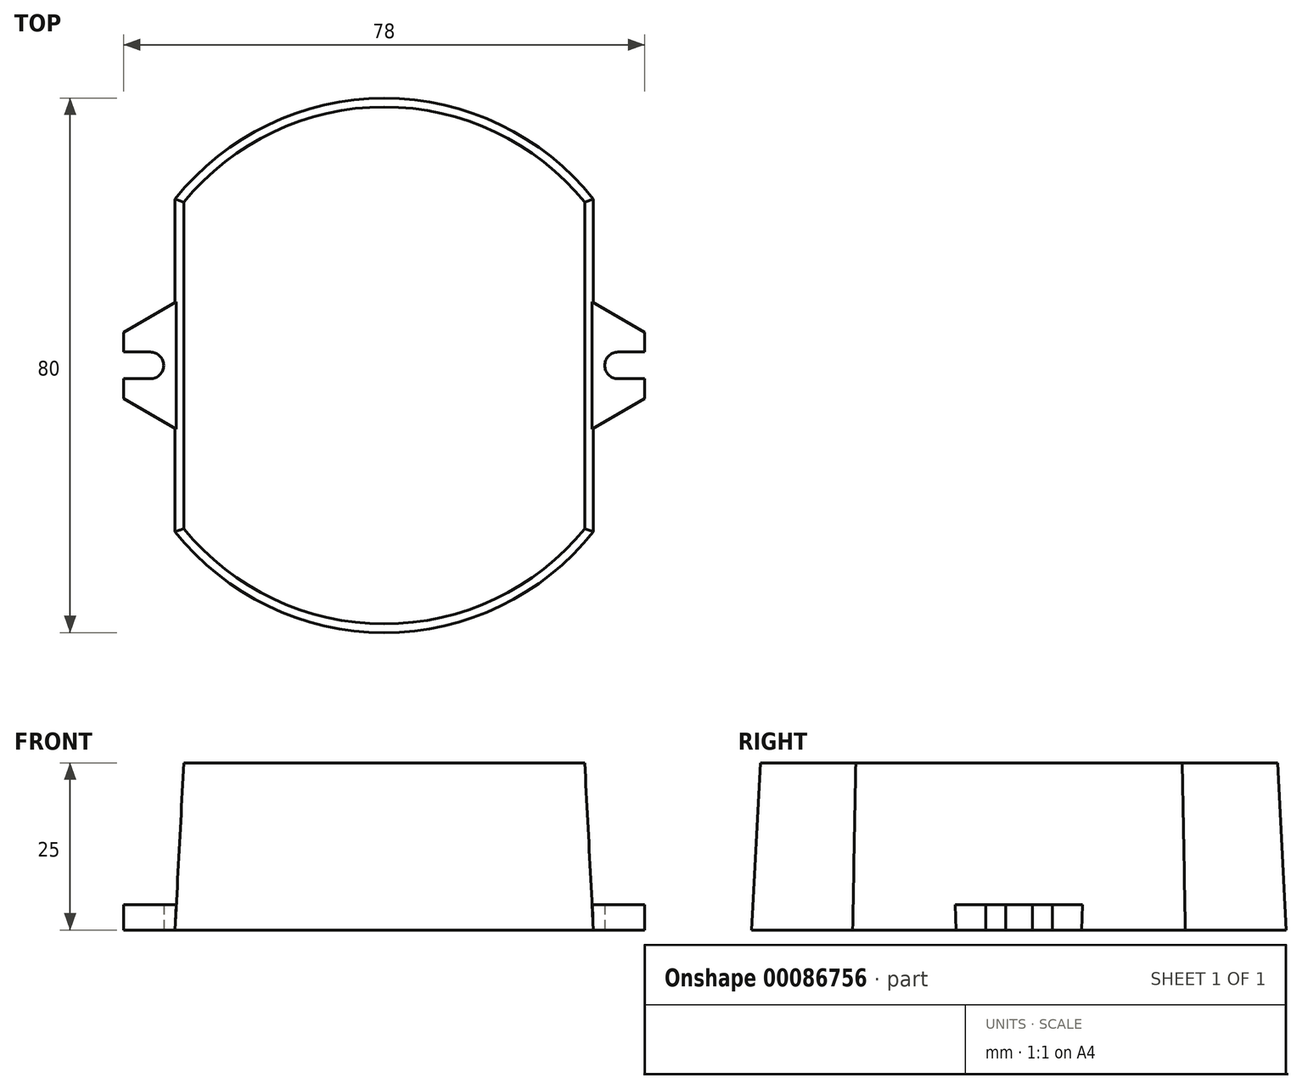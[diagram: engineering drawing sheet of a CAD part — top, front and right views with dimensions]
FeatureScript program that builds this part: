
annotation { "Feature Type Name" : "Feature", "Feature Type Description" : "" }
export const myFeature = defineFeature(function(context is Context, id is Id, definition is map)
    precondition{}
    {
        {
            var Q0;
            Q0=qCreatedBy(makeId("Top.planeOp"),FACE);
            var sketch = newSketch(context, id + "F0", { "sketchPlane" : qUnion([Q0])});
            skCircle(sketch, "E0", {"center": v(0, 0) * mm, "radius": 40 * mm});
            skSolve(sketch);
        }
        {
            var Q0;
            Q0 = qSketchRegion(id + "F0", true);
            extrude(context, id + "F1", {"entities" : qUnion([Q0]), "depth" : 25 * mm, "hasDraft" : true, "draftAngle" : 3 * degree, "draftPullDirection" : true});
        }
        {
            var Q0;
            Q0=makeQuery(id+"F1.opExtrude","CAP_FACE",FACE,{"disambiguationData":[OSD([sQuery(id+"F0.wireOp",EDGE,"E0")])],"isStart":false});
            var sketch = newSketch(context, id + "F2", { "sketchPlane" : qUnion([Q0])});
            skLineSegment(sketch, "E1.bottom", {"start": v(-30, 50.8) * mm, "end": v(-55.4, 50.8) * mm});
            skLineSegment(sketch, "E1.top", {"start": v(-30, -50.8) * mm, "end": v(-55.4, -50.8) * mm});
            skLineSegment(sketch, "E1.left", {"start": v(-30, 50.8) * mm, "end": v(-30, -50.8) * mm});
            skLineSegment(sketch, "E1.right", {"start": v(-55.4, 50.8) * mm, "end": v(-55.4, -50.8) * mm});
            skLineSegment(sketch, "E2", {"start": v(0, 0) * mm, "end": v(-67.46, 0) * mm, "construction": true});
            skLineSegment(sketch, "E3", {"start": v(0, 0) * mm, "end": v(0, 59.02) * mm, "construction": true});
            skLineSegment(sketch, "E4.MirrorCS", {"start": v(0, 0) * mm, "end": v(67.46, 0) * mm, "construction": true});
            skLineSegment(sketch, "E5.MirrorCS", {"start": v(55.4, 50.8) * mm, "end": v(55.4, -50.8) * mm});
            skLineSegment(sketch, "E6.MirrorCS", {"start": v(30, 50.8) * mm, "end": v(55.4, 50.8) * mm});
            skLineSegment(sketch, "E7.MirrorCS", {"start": v(30, 50.8) * mm, "end": v(30, -50.8) * mm});
            skLineSegment(sketch, "E8.MirrorCS", {"start": v(30, -50.8) * mm, "end": v(55.4, -50.8) * mm});
            skSolve(sketch);
        }
        {
            var Q0;
            Q0 = qSketchRegion(id + "F2", true);
            extrude(context, id + "F3", {"entities" : qUnion([Q0]), "operationType" : NewBodyOperationType.REMOVE, "endBound" : BoundingType.THROUGH_ALL, "oppositeDirection" : true, "depth" : 25.4 * mm, "hasDraft" : true, "draftAngle" : 3 * degree, "draftPullDirection" : true});
        }
        {
            var Q0;
            Q0=makeQuery(id+"F1.opExtrude","CAP_FACE",FACE,{"disambiguationData":[OSD([sQuery(id+"F0.wireOp",EDGE,"E0")])],"isStart":true});
            var sketch = newSketch(context, id + "F4", { "sketchPlane" : qUnion([Q0])});
            skLineSegment(sketch, "E9", {"start": v(0, 0) * mm, "end": v(0, -36.6) * mm, "construction": true});
            skArc(sketch, "E10", {"start": v(-33, 0) * mm, "mid": v(-33.59, 1.41) * mm, "end": v(-35, 2) * mm});
            skLineSegment(sketch, "E11", {"start": v(-35, 2) * mm, "end": v(-39, 2) * mm});
            skLineSegment(sketch, "E12", {"start": v(-39, 2) * mm, "end": v(-39, 4.96) * mm});
            skLineSegment(sketch, "E13", {"start": v(-39, 4.96) * mm, "end": v(-30, 10.16) * mm});
            skLineSegment(sketch, "E14", {"start": v(0, 0) * mm, "end": v(-53.11, 0) * mm, "construction": true});
            skArc(sketch, "E15.MirrorCS", {"start": v(-33, 0) * mm, "mid": v(-33.59, -1.41) * mm, "end": v(-35, -2) * mm});
            skLineSegment(sketch, "E16.MirrorCS", {"start": v(-39, -2) * mm, "end": v(-39, -4.96) * mm});
            skLineSegment(sketch, "E17.MirrorCS", {"start": v(-39, -4.96) * mm, "end": v(-30, -10.16) * mm});
            skLineSegment(sketch, "E18.MirrorCS", {"start": v(-35, -2) * mm, "end": v(-39, -2) * mm});
            skLineSegment(sketch, "E19", {"start": v(-30, -10.16) * mm, "end": v(-30, 10.16) * mm});
            skLineSegment(sketch, "E20.MirrorCS", {"start": v(35, 2) * mm, "end": v(39, 2) * mm});
            skArc(sketch, "E21.MirrorCS", {"start": v(33, 0) * mm, "mid": v(33.59, 1.41) * mm, "end": v(35, 2) * mm});
            skLineSegment(sketch, "E22.MirrorCS", {"start": v(39, 2) * mm, "end": v(39, 4.96) * mm});
            skArc(sketch, "E23.MirrorCS", {"start": v(33, 0) * mm, "mid": v(33.59, -1.41) * mm, "end": v(35, -2) * mm});
            skLineSegment(sketch, "E24.MirrorCS", {"start": v(39, -2) * mm, "end": v(39, -4.96) * mm});
            skLineSegment(sketch, "E25.MirrorCS", {"start": v(35, -2) * mm, "end": v(39, -2) * mm});
            skLineSegment(sketch, "E26.MirrorCS", {"start": v(39, 4.96) * mm, "end": v(30, 10.16) * mm});
            skLineSegment(sketch, "E27.MirrorCS", {"start": v(0, 0) * mm, "end": v(53.11, 0) * mm, "construction": true});
            skLineSegment(sketch, "E28.MirrorCS", {"start": v(39, -4.96) * mm, "end": v(30, -10.16) * mm});
            skLineSegment(sketch, "E29.MirrorCS", {"start": v(30, -10.16) * mm, "end": v(30, 10.16) * mm});
            skSolve(sketch);
        }
        {
            var Q0;
            Q0 = qSketchRegion(id + "F4", true);
            extrude(context, id + "F5", {"entities" : qUnion([Q0]), "operationType" : NewBodyOperationType.ADD, "oppositeDirection" : true, "depth" : 3.8 * mm});
        }
    });
